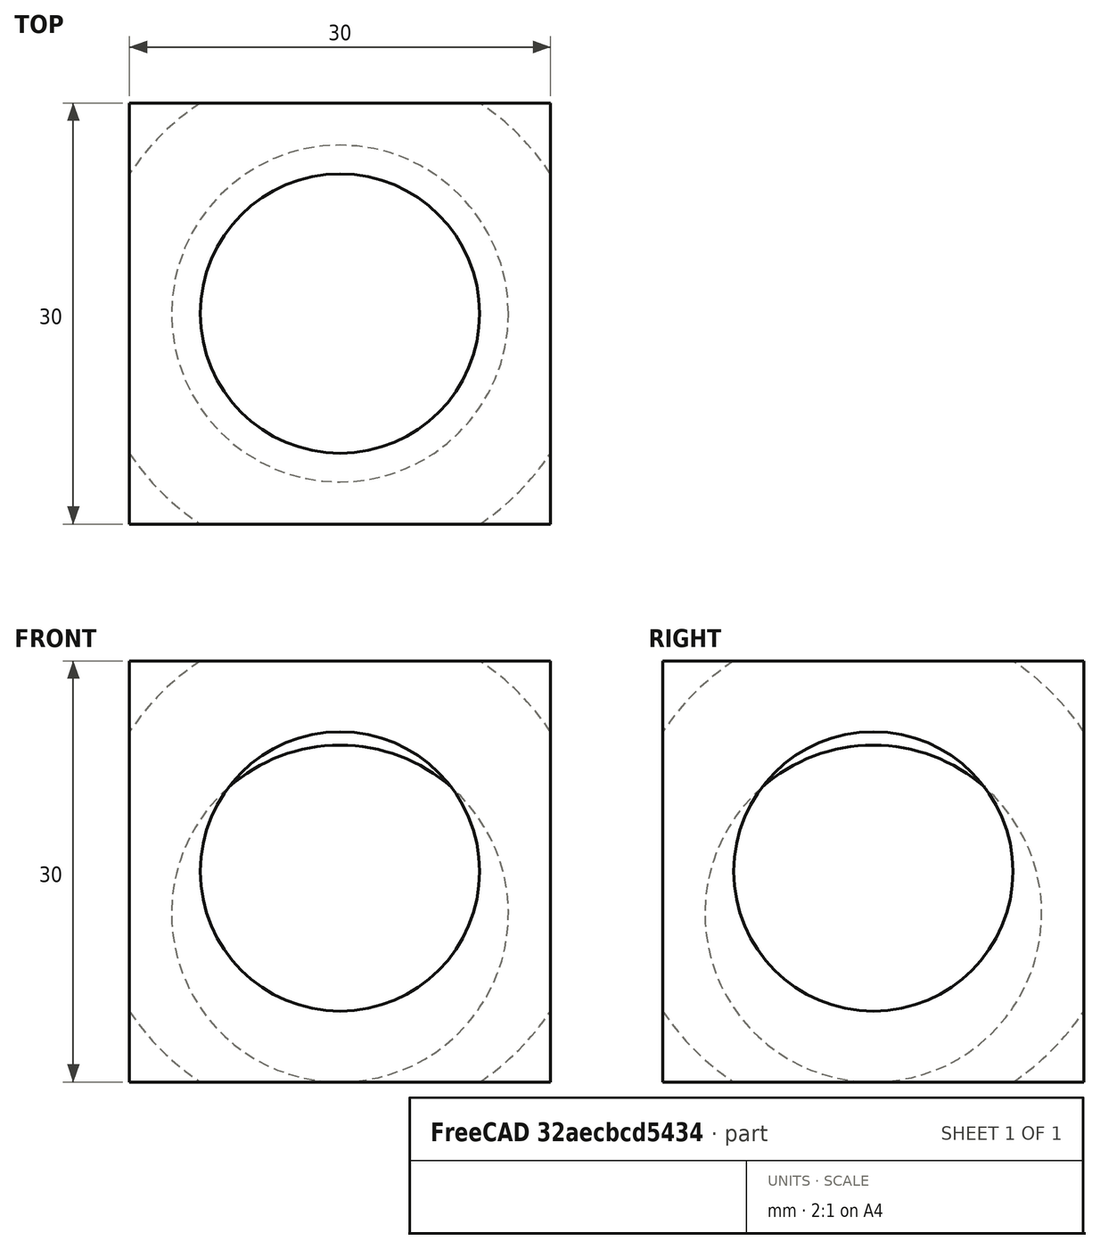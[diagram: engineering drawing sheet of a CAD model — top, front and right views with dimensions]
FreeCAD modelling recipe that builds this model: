
FCSTD DOCUMENT  (FreeCAD 0.21R33694 (Git))
Label: npatris_repte1
License: All rights reserved
LicenseURL: https://en.wikipedia.org/wiki/All_rights_reserved
objects: Part::Sphere×2, Part::Box×1, Part::Cut×1, Part::MultiFuse×1
note: 5 computed .brp shape members not serialized (recipe doc carries the construction recipe); baked Part::Feature solids carry a one-line shape summary decoded from their .brp

FEATURE [Part::Box] Box  label="Cub"
  AttacherType = Attacher::AttachEngine3D
  Height = 30
  Length = 30
  Width = 30
FEATURE [Part::Sphere] Sphere  label="Esfera"
  Angle1 = -90
  Angle2 = 90
  Angle3 = 360
  AttacherType = Attacher::AttachEngine3D
  Placement = pos=(15,15,15) rot=(0,0,1;0rad)
  Radius = 18
FEATURE [Part::Cut] Cut  label="Quadrat amb forats"
  Base = -> Box
  Tool = -> Sphere
FEATURE [Part::Sphere] Sphere001  label="Esfera_interior"
  Angle1 = -90
  Angle2 = 90
  Angle3 = 360
  AttacherType = Attacher::AttachEngine3D
  Placement = pos=(15,15,12) rot=(0,0,1;0rad)
  Radius = 12
FEATURE [Part::MultiFuse] Fusion  label="Quadrat_amb_esfera_interior"
  Shapes = -> [Cut,Sphere001]
